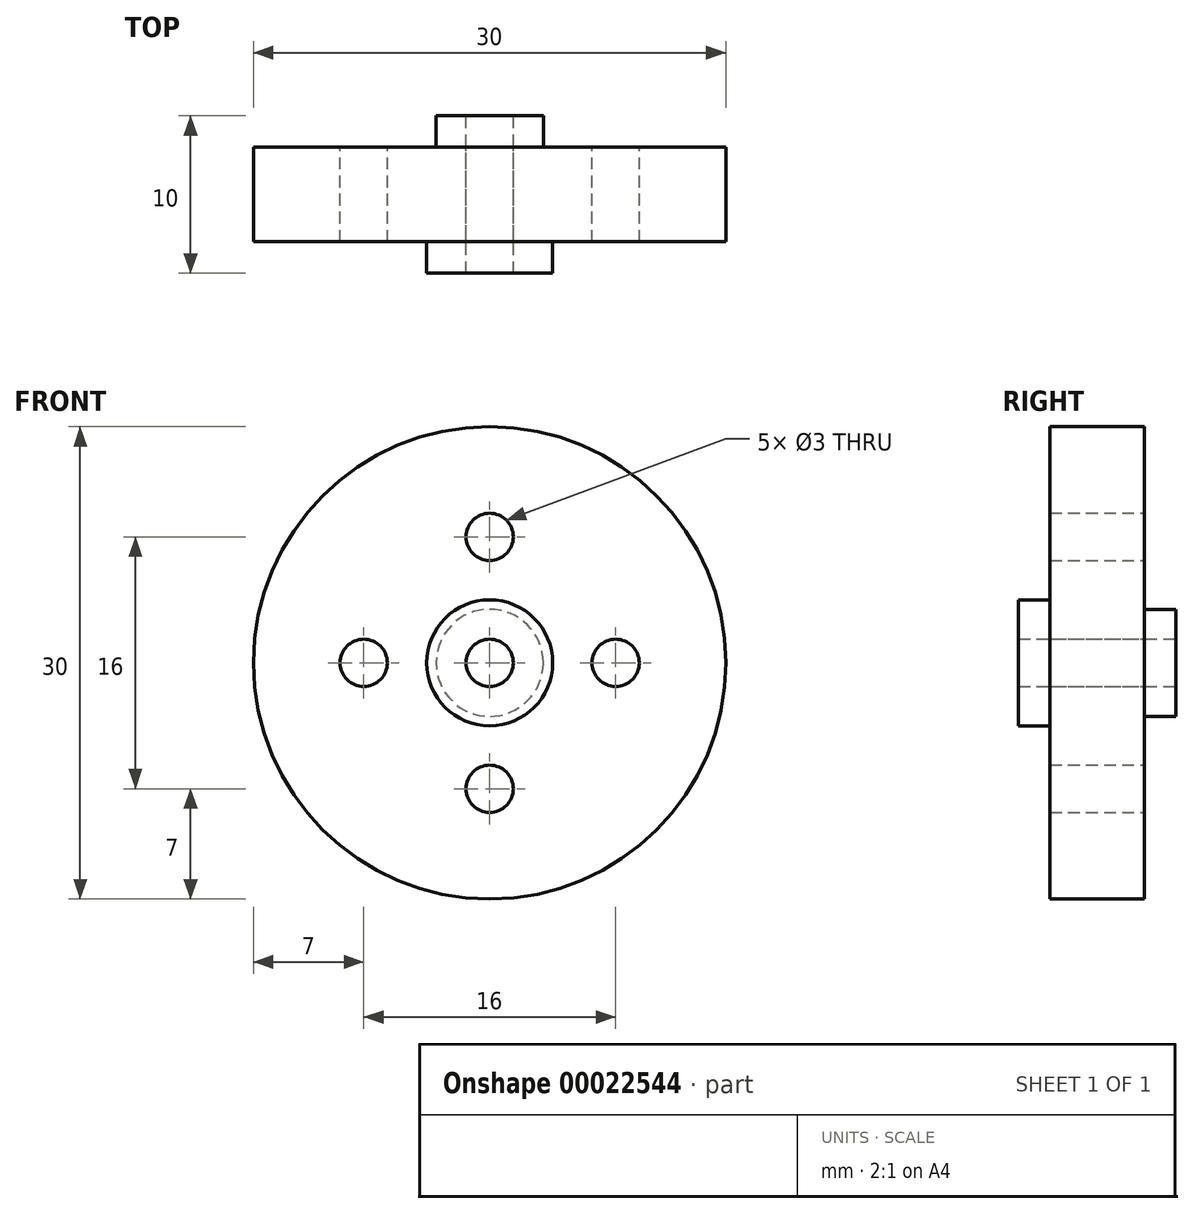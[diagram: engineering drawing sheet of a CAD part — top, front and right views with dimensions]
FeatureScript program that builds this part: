
annotation { "Feature Type Name" : "Feature", "Feature Type Description" : "" }
export const myFeature = defineFeature(function(context is Context, id is Id, definition is map)
    precondition{}
    {
        {
            var Q0;
            Q0=qCreatedBy(makeId("Front.planeOp"),FACE);
            var sketch = newSketch(context, id + "F0", { "sketchPlane" : qUnion([Q0])});
            skCircle(sketch, "E0", {"center": v(0, 0) * mm, "radius": 15 * mm});
            skCircle(sketch, "E1", {"center": v(0, 0) * mm, "radius": 4 * mm});
            skCircle(sketch, "E2", {"center": v(0, 0) * mm, "radius": 1.5 * mm});
            skCircle(sketch, "E3", {"center": v(0, 8) * mm, "radius": 1.5 * mm});
            skCircle(sketch, "E4.1.0", {"center": v(-8, 0) * mm, "radius": 1.5 * mm});
            skCircle(sketch, "E4.2.0", {"center": v(0, -8) * mm, "radius": 1.5 * mm});
            skCircle(sketch, "E4.3.0", {"center": v(8, 0) * mm, "radius": 1.5 * mm});
            skSolve(sketch);
        }
        {
            var Q0;
            Q0=makeQuery(id+"F0.imprint","IMPRINT",FACE,{"disambiguationData":[TD([[makeQuery(id+"F0.imprint","IMPRINT",EDGE,{"derivedFrom":sQuery(id+"F0.wireOp",EDGE,"E0")}),1.0]])]});
            extrude(context, id + "F1", {"entities" : qUnion([Q0]), "depth" : 6 * mm});
        }
        {
            var Q0;
            Q0=makeQuery(id+"F0.imprint","IMPRINT",FACE,{"disambiguationData":[TD([[makeQuery(id+"F0.imprint","IMPRINT",EDGE,{"derivedFrom":sQuery(id+"F0.wireOp",EDGE,"E1")}),1.0]])]});
            extrude(context, id + "F2", {"entities" : qUnion([Q0]), "operationType" : NewBodyOperationType.ADD, "depth" : 8 * mm});
        }
        {
            var Q0;
            {var subQ0=sQuery(id+"F0.wireOp",EDGE,"E1");Q0=makeQuery(id+"F2.boolean.opBoolean","MERGE",FACE,{"derivedFrom":[makeQuery(id+"F1.opExtrude","CAP_FACE",FACE,{"disambiguationData":[OSD([sQuery(id+"F0.wireOp",EDGE,"E0"),subQ0,sQuery(id+"F0.wireOp",EDGE,"E3"),sQuery(id+"F0.wireOp",EDGE,"E4.1.0"),sQuery(id+"F0.wireOp",EDGE,"E4.2.0"),sQuery(id+"F0.wireOp",EDGE,"E4.3.0")])],"isStart":true}),makeQuery(id+"F2.opExtrude","CAP_FACE",FACE,{"disambiguationData":[OSD([subQ0,sQuery(id+"F0.wireOp",EDGE,"E2")])],"isStart":true})]});}
            var sketch = newSketch(context, id + "F3", { "sketchPlane" : qUnion([Q0])});
            skCircle(sketch, "E5", {"center": v(0, 0) * mm, "radius": 3.4 * mm});
            skSolve(sketch);
        }
        {
            var Q0;
            Q0=makeQuery(id+"F3.imprint","IMPRINT",FACE,{"disambiguationData":[TD([[makeQuery(id+"F3.imprint","IMPRINT",EDGE,{"derivedFrom":sQuery(id+"F3.wireOp",EDGE,"E5")}),1.0]])]});
            extrude(context, id + "F4", {"entities" : qUnion([Q0]), "operationType" : NewBodyOperationType.ADD, "depth" : 2 * mm});
        }
    });
